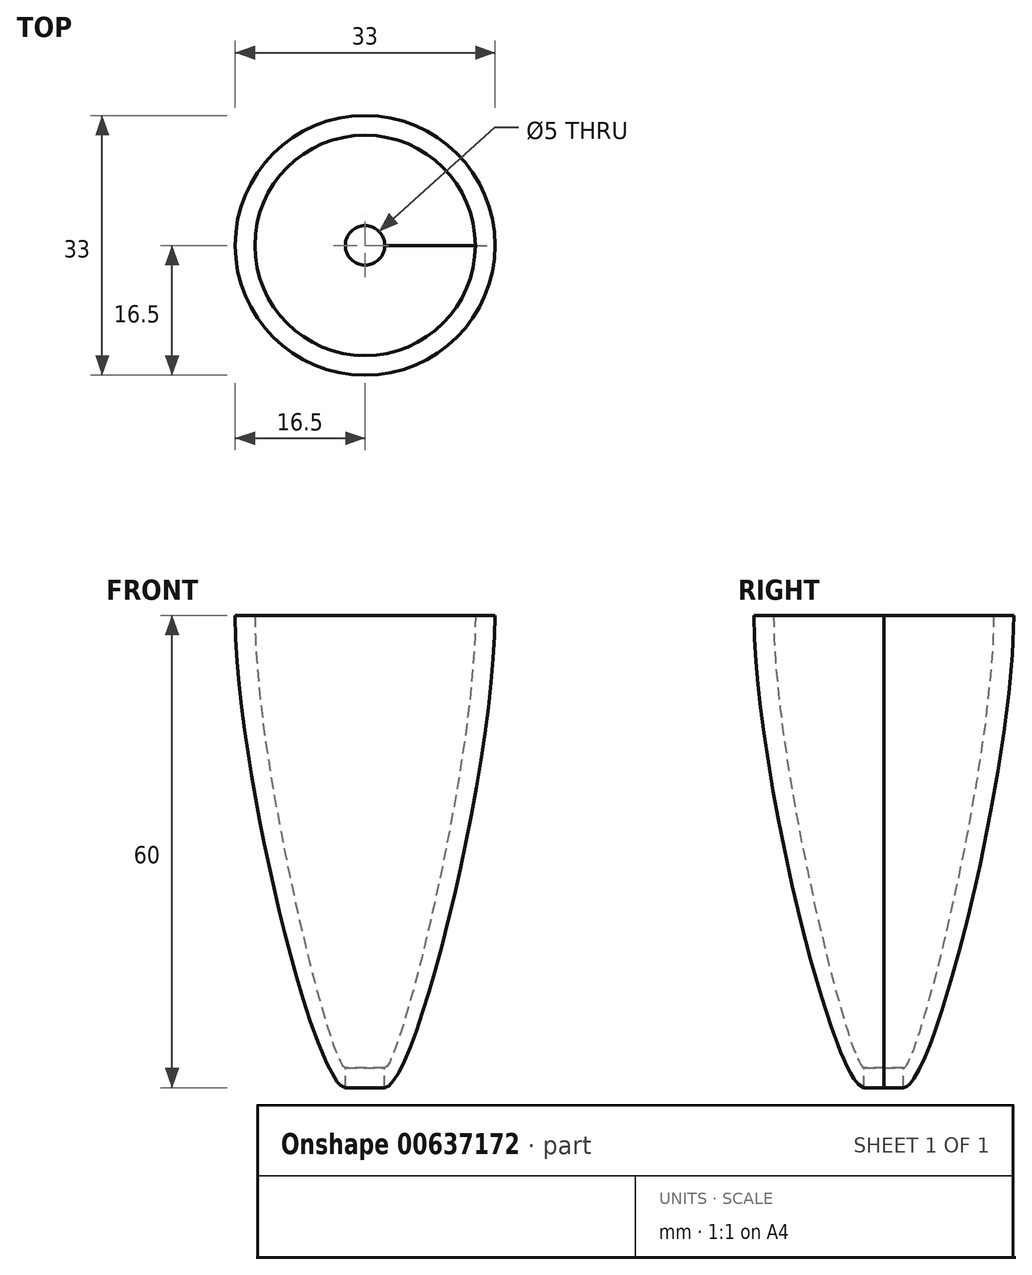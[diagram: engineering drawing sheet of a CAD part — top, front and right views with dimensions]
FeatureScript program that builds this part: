
annotation { "Feature Type Name" : "Feature", "Feature Type Description" : "" }
export const myFeature = defineFeature(function(context is Context, id is Id, definition is map)
    precondition{}
    {
        {
            var Q0;
            Q0=qCreatedBy(makeId("Front.planeOp"),FACE);
            var sketch = newSketch(context, id + "F0", { "sketchPlane" : qUnion([Q0])});
            skFitSpline(sketch, "E0", {"points": [v(-2.5, -52.8) * mm, v(-16.5, 7.2) * mm], "startDerivative": vector(-11.69, 0.28) * mm, "endDerivative": vector(0, 57.92) * mm});
            skLineSegment(sketch, "E1", {"start": v(-16.5, 7.2) * mm, "end": v(-14, 7.2) * mm});
            skLineSegment(sketch, "E2", {"start": v(-2.5, -52.8) * mm, "end": v(-2.5, -50.3) * mm});
            skFitSpline(sketch, "E3", {"points": [v(-14, 7.2) * mm, v(-2.5, -50.3) * mm], "startDerivative": vector(0, -57.92) * mm, "endDerivative": vector(5.55, 0.3) * mm});
            skLineSegment(sketch, "E4", {"start": v(0, 9.04) * mm, "end": v(0, -42.06) * mm, "construction": true});
            skSolve(sketch);
        }
        {
            var Q0;
            Q0=qSketchRegion(id+"F0",true);
            var Q1;
            Q1=sQuery(id+"F0.wireOp",EDGE,"E4");
            revolve(context, id + "F1", {"entities" : qUnion([Q0]), "axis" : qUnion([Q1]), "revolveType" : RevolveType.FULL});
        }
    });
